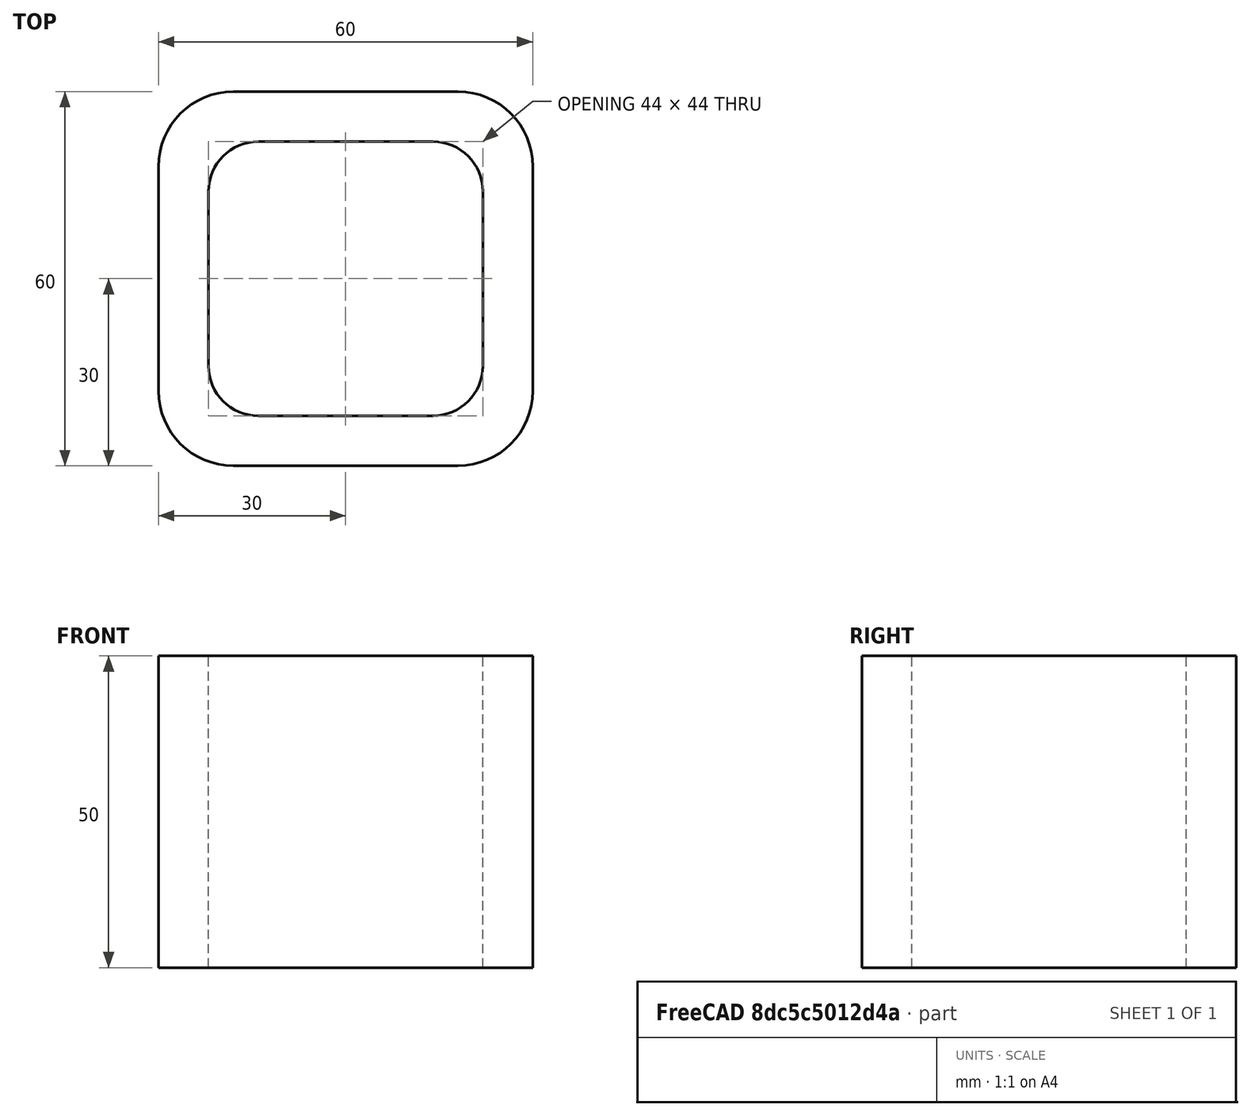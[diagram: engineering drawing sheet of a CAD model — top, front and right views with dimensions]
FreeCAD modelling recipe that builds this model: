
FCSTD DOCUMENT  (FreeCAD 0.15R4671 (Git))
Label: Square hollow section 60x60x8 EN10219 S235JRH
License: All rights reserved
LicenseURL: http://en.wikipedia.org/wiki/All_rights_reserved
objects: Sketcher::SketchObject×1, Part::Extrusion×1
note: 2 computed .brp shape members not serialized (recipe doc carries the construction recipe); baked Part::Feature solids carry a one-line shape summary decoded from their .brp

FEATURE [Sketcher::SketchObject] Sketch
  sketch-geometry (16):
    g0: LineSegment StartX=-14 StartY=22 StartZ=0 EndX=14 EndY=22 EndZ=0
    g1: LineSegment StartX=22 StartY=14 StartZ=0 EndX=22 EndY=-14 EndZ=0
    g2: LineSegment StartX=14 StartY=-22 StartZ=0 EndX=-14 EndY=-22 EndZ=0
    g3: LineSegment StartX=-22 StartY=-14 StartZ=0 EndX=-22 EndY=14 EndZ=0
    g4: LineSegment StartX=-18 StartY=30 StartZ=0 EndX=18 EndY=30 EndZ=0
    g5: LineSegment StartX=30 StartY=18 StartZ=0 EndX=30 EndY=-18 EndZ=0
    g6: LineSegment StartX=18 StartY=-30 StartZ=0 EndX=-18 EndY=-30 EndZ=0
    g7: LineSegment StartX=-30 StartY=-18 StartZ=0 EndX=-30 EndY=18 EndZ=0
    g8: ArcOfCircle CenterX=-14 CenterY=14 CenterZ=0 NormalX=0 NormalY=0 NormalZ=1 Radius=8 StartAngle=1.5708 EndAngle=3.14159
    g9: ArcOfCircle CenterX=14 CenterY=14 CenterZ=0 NormalX=0 NormalY=0 NormalZ=1 Radius=8 StartAngle=0 EndAngle=1.5708
    g10: ArcOfCircle CenterX=14 CenterY=-14 CenterZ=0 NormalX=0 NormalY=0 NormalZ=1 Radius=8 StartAngle=4.71239 EndAngle=6.28319
    g11: ArcOfCircle CenterX=-14 CenterY=-14 CenterZ=0 NormalX=0 NormalY=0 NormalZ=1 Radius=8 StartAngle=3.14159 EndAngle=4.71239
    g12: ArcOfCircle CenterX=18 CenterY=18 CenterZ=0 NormalX=0 NormalY=0 NormalZ=1 Radius=12 StartAngle=0 EndAngle=1.5708
    g13: ArcOfCircle CenterX=18 CenterY=-18 CenterZ=0 NormalX=0 NormalY=0 NormalZ=1 Radius=12 StartAngle=4.71239 EndAngle=6.28319
    g14: ArcOfCircle CenterX=-18 CenterY=-18 CenterZ=0 NormalX=0 NormalY=0 NormalZ=1 Radius=12 StartAngle=3.14159 EndAngle=4.71239
    g15: ArcOfCircle CenterX=-18 CenterY=18 CenterZ=0 NormalX=0 NormalY=0 NormalZ=1 Radius=12 StartAngle=1.5708 EndAngle=3.14159
  constraints (36):
    c: Horizontal(g2)
    c: Vertical(g3)
    c: Horizontal(g6)
    c: Vertical(g7)
    c: Tangent(g3,g8) = 1.5708
    c: Tangent(g0,g8) = 1.5708
    c: Tangent(g0,g9) = 1.5708
    c: Tangent(g1,g9) = 1.5708
    c: Tangent(g1,g10) = 1.5708
    c: Tangent(g2,g10) = 1.5708
    c: Tangent(g2,g11) = 1.5708
    c: Tangent(g3,g11) = 1.5708
    c: Tangent(g4,g12) = 1.5708
    c: Tangent(g5,g12) = 1.5708
    c: Tangent(g5,g13) = 1.5708
    c: Tangent(g6,g13) = 1.5708
    c: Tangent(g6,g14) = 1.5708
    c: Tangent(g7,g14) = 1.5708
    c: Tangent(g7,g15) = 1.5708
    c: Tangent(g4,g15) = 1.5708
    c: Equal(g9,g8)
    c: Equal(g9,g11)
    c: Equal(g9,g10)
    c: Equal(g12,g15)
    c: Equal(g12,g14)
    c: Equal(g12,g13)
    c: Symmetric(g4,g6,g-1)
    c: Symmetric(g7,g5,g-2)
    c: DistanceY(g4,g6) = -60
    c: DistanceX(g7,g5) = 60
    c: Symmetric(g3,g1,g-2)
    c: Symmetric(g0,g2,g-1)
    c: DistanceY(g0,g4) = 8
    c: DistanceX(g5,g1) = -8
    c: Radius(g9) = 8
    c: Radius(g12) = 12
FEATURE [Part::Extrusion] Extrude  label="Square hollow section 60x60x8 EN10219 S235JRH"
  Base = -> Sketch
  Dir = (0,0,50)
  Solid = true
